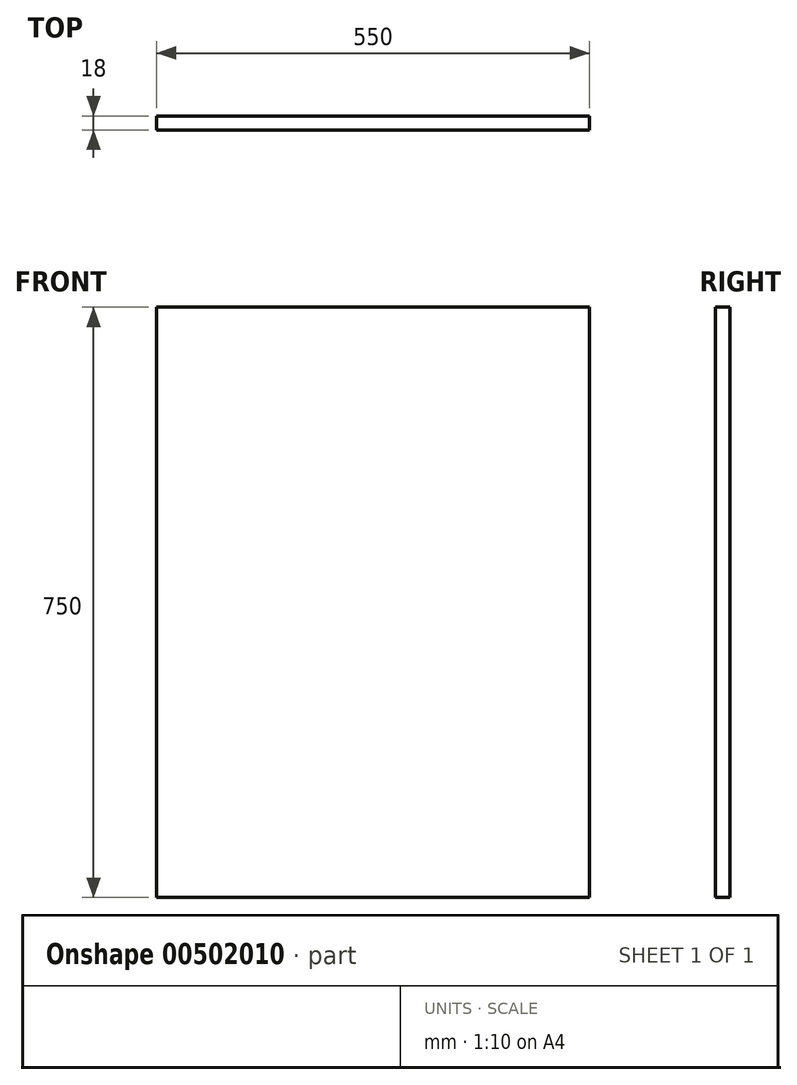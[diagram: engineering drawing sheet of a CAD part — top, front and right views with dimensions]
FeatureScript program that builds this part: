
annotation { "Feature Type Name" : "Feature", "Feature Type Description" : "" }
export const myFeature = defineFeature(function(context is Context, id is Id, definition is map)
    precondition{}
    {
        {
            var Q0;
            Q0=qCreatedBy(makeId("Front.planeOp"),FACE);
            var sketch = newSketch(context, id + "F0", { "sketchPlane" : qUnion([Q0])});
            skLineSegment(sketch, "E0.bottom", {"start": v(0, 0) * mm, "end": v(550, 0) * mm});
            skLineSegment(sketch, "E0.top", {"start": v(0, 750) * mm, "end": v(550, 750) * mm});
            skLineSegment(sketch, "E0.left", {"start": v(0, 0) * mm, "end": v(0, 750) * mm});
            skLineSegment(sketch, "E0.right", {"start": v(550, 0) * mm, "end": v(550, 750) * mm});
            skSolve(sketch);
        }
        {
            var Q0;
            Q0=makeQuery(id+"F0.imprint","IMPRINT",FACE,{"disambiguationData":[TD([[makeQuery(id+"F0.imprint","IMPRINT",EDGE,{"derivedFrom":sQuery(id+"F0.wireOp",EDGE,"E0.bottom")}),1.0]])]});
            extrude(context, id + "F1", {"entities" : qUnion([Q0]), "depth" : 18 * mm});
        }
    });
